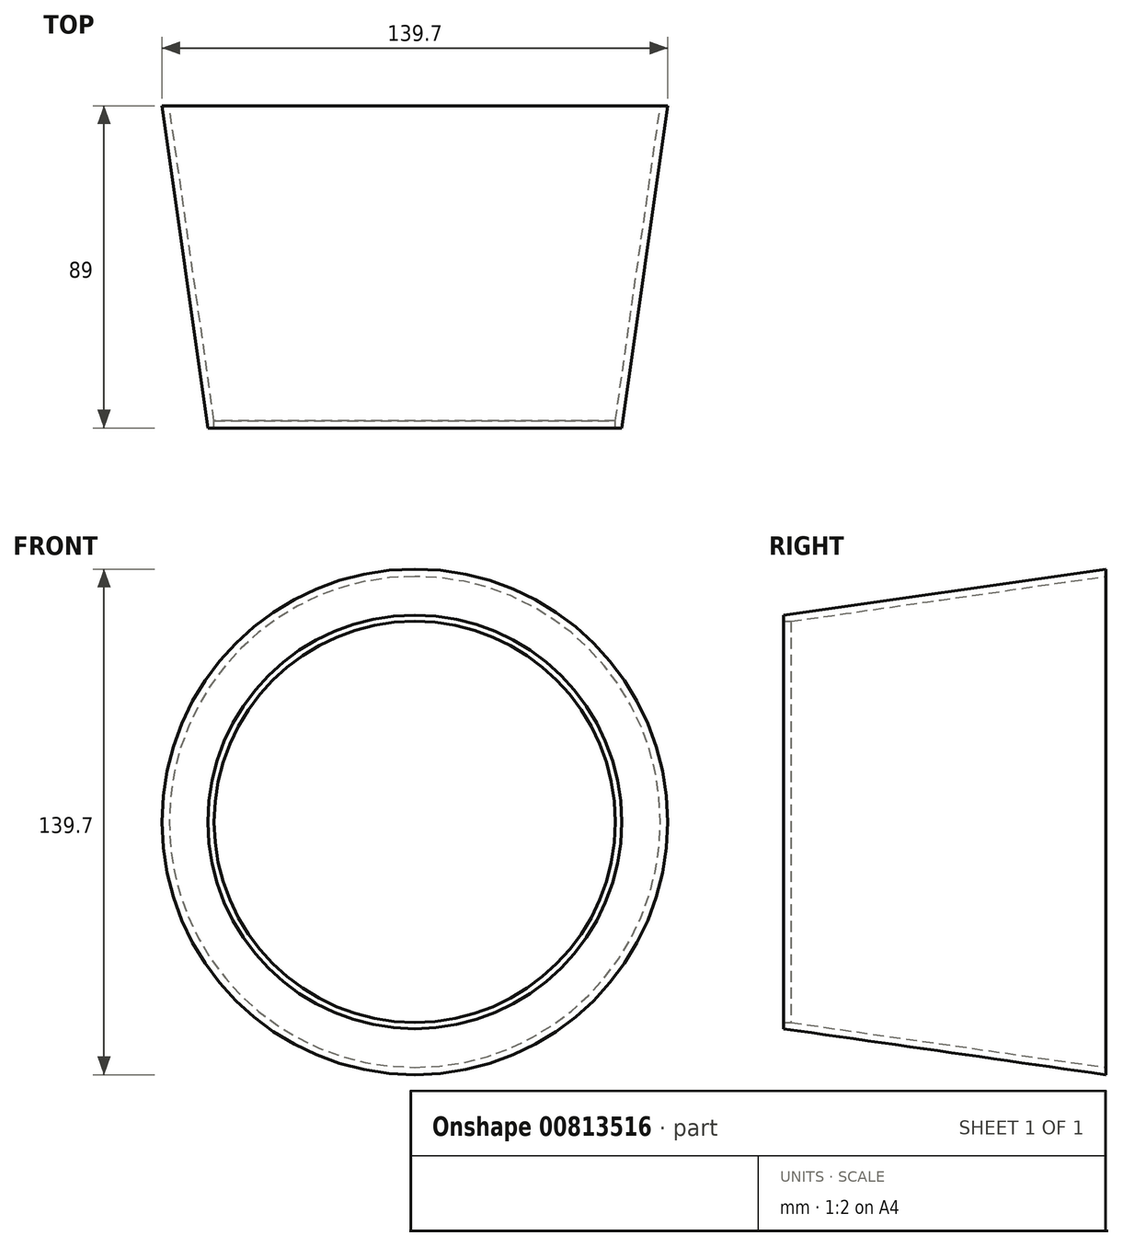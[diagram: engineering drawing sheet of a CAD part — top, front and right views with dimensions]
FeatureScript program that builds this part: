
annotation { "Feature Type Name" : "Feature", "Feature Type Description" : "" }
export const myFeature = defineFeature(function(context is Context, id is Id, definition is map)
    precondition{}
    {
        {
            var Q0;
            Q0=qCreatedBy(makeId("Front.planeOp"),FACE);
            var sketch = newSketch(context, id + "F0", { "sketchPlane" : qUnion([Q0])});
            skCircle(sketch, "E0", {"center": v(0, 0) * mm, "radius": 69.85 * mm});
            skSolve(sketch);
        }
        {
            var Q0;
            Q0=qCreatedBy(makeId("Front.planeOp"),FACE);
            cPlane(context, id + "F1", {"entities" : qUnion([Q0]), "cplaneType" : CPlaneType.OFFSET, "offset" : 89 * mm, "width" : 150 * mm, "height" : 150 * mm});
        }
        {
            var Q0;
            Q0=qCreatedBy(id+"F1.planeOp",FACE);
            var sketch = newSketch(context, id + "F2", { "sketchPlane" : qUnion([Q0])});
            skCircle(sketch, "E1", {"center": v(0, 0) * mm, "radius": 57.15 * mm});
            skSolve(sketch);
        }
        {
            var Q0;
            Q0=makeQuery(id+"F0.imprint","IMPRINT",FACE,{"disambiguationData":[TD([[makeQuery(id+"F0.imprint","IMPRINT",EDGE,{"derivedFrom":sQuery(id+"F0.wireOp",EDGE,"E0")}),1.0]])]});
            var Q1;
            Q1=makeQuery(id+"F2.imprint","IMPRINT",FACE,{"disambiguationData":[TD([[makeQuery(id+"F2.imprint","IMPRINT",EDGE,{"derivedFrom":sQuery(id+"F2.wireOp",EDGE,"E1")}),1.0]])]});
            loft(context, id + "F3", {"sheetProfilesArray" : [{ "sheetProfileEntities" : qUnion([Q0]) }, { "sheetProfileEntities" : qUnion([Q1]) }]});
        }
        {
            var Q0;
            Q0=makeQuery(id+"F3.opLoft","CAP_FACE",FACE,{"disambiguationData":[OSD([makeQuery(id+"F0.imprint","IMPRINT",FACE,{"disambiguationData":[TD([[makeQuery(id+"F0.imprint","IMPRINT",EDGE,{"derivedFrom":sQuery(id+"F0.wireOp",EDGE,"E0")}),1.0]])]})])],"isStart":true});
            shell(context, id + "F4", {"entities" : qUnion([Q0]), "thickness" : 2 * mm});
        }
        {
            var Q0;
            Q0=qCreatedBy(makeId("Right.planeOp"),FACE);
            var sketch = newSketch(context, id + "F5", { "sketchPlane" : qUnion([Q0])});
            skLineSegment(sketch, "E2", {"start": v(-107.46, 0) * mm, "end": v(-52.55, 0) * mm});
            skSolve(sketch);
        }
        {
            var Q0;
            Q0=makeQuery(id+"F4.opShell","OFFSET_FACE",FACE,{"disambiguationData":[OSD([makeQuery(id+"F2.imprint","IMPRINT",FACE,{"disambiguationData":[TD([[makeQuery(id+"F2.imprint","IMPRINT",EDGE,{"derivedFrom":sQuery(id+"F2.wireOp",EDGE,"E1")}),1.0]])]})])]});
            var Q1;
            Q1=sQuery(id+"F5.wireOp",EDGE,"E2");
            sweep(context, id + "F6", {"operationType" : NewBodyOperationType.REMOVE, "profiles" : qUnion([Q0]), "path" : qUnion([Q1])});
        }
    });
